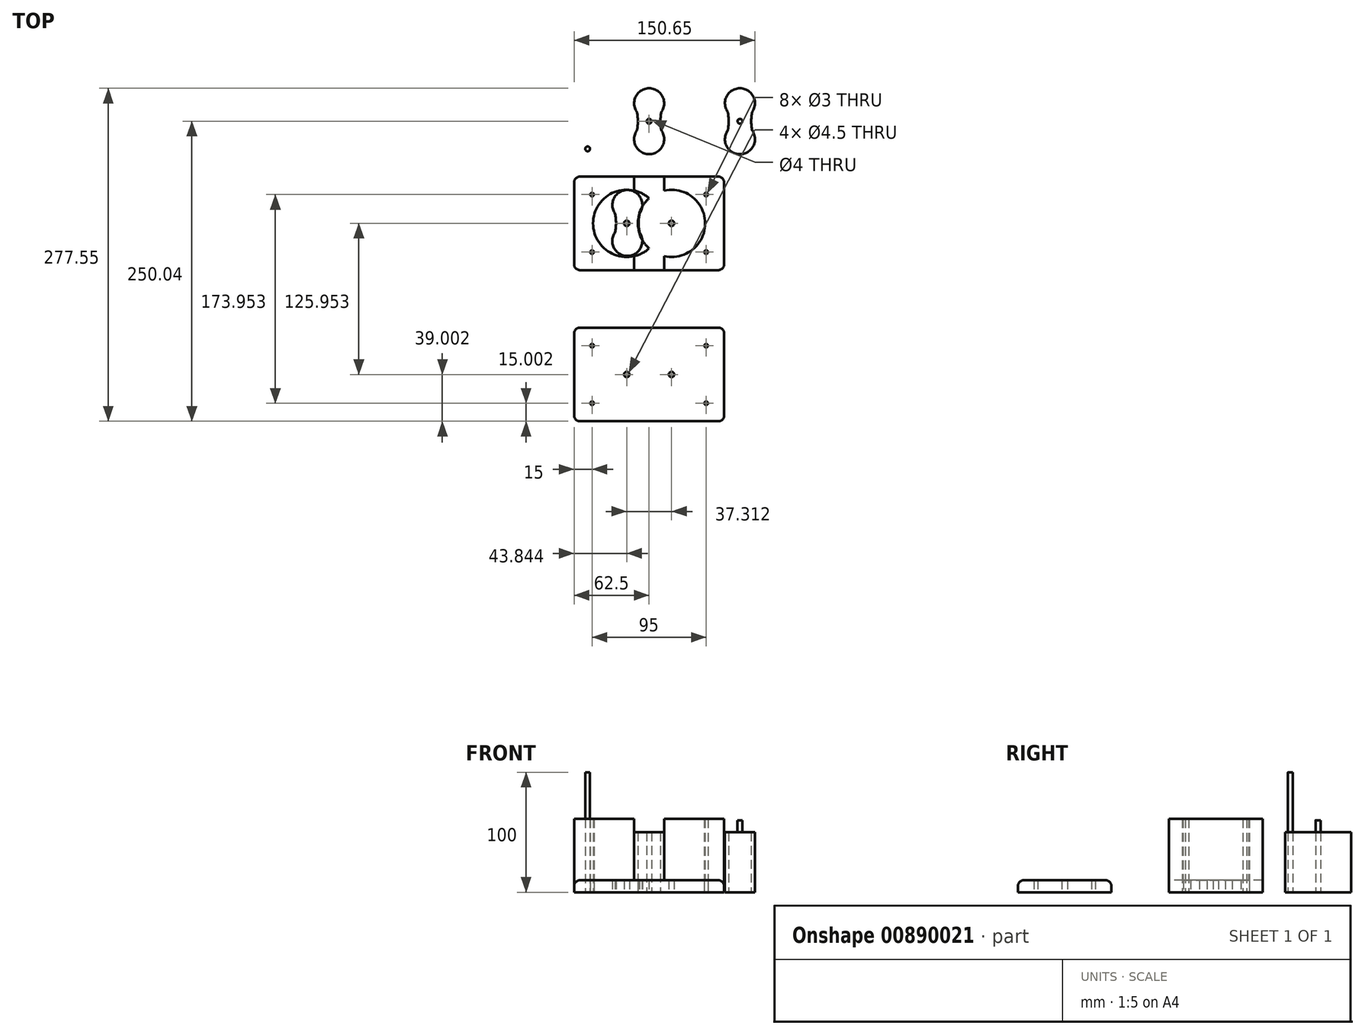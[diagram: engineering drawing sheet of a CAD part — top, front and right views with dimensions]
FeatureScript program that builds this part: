
annotation { "Feature Type Name" : "Feature", "Feature Type Description" : "" }
export const myFeature = defineFeature(function(context is Context, id is Id, definition is map)
    precondition{}
    {
        {
            var Q0;
            Q0=qCreatedBy(makeId("Top.planeOp"),FACE);
            var sketch = newSketch(context, id + "F0", { "sketchPlane" : qUnion([Q0])});
            skArc(sketch, "E0", {"start": v(-10.1, -7.63) * mm, "mid": v(0, -27.5) * mm, "end": v(10.1, -7.63) * mm});
            skArc(sketch, "E1", {"start": v(10.1, 7.63) * mm, "mid": v(0, 27.5) * mm, "end": v(-10.1, 7.64) * mm});
            skLineSegment(sketch, "E2", {"start": v(0, 107.1) * mm, "end": v(0, -296.82) * mm, "construction": true});
            skArc(sketch, "E3", {"start": v(10.1, 7.63) * mm, "mid": v(9.42, 0) * mm, "end": v(10.1, -7.63) * mm});
            skArc(sketch, "E4.trimOffspring", {"start": v(-10.1, -7.63) * mm, "mid": v(-9.43, 0) * mm, "end": v(-10.1, 7.64) * mm});
            skPoint(sketch, "E5.center.orphan", {"position": v(-53, 0) * mm});
            skCircle(sketch, "E6", {"center": v(18.66, -85.09) * mm, "radius": 28 * mm});
            skCircle(sketch, "E7", {"center": v(-18.66, -85.09) * mm, "radius": 28 * mm});
            skLineSegment(sketch, "E8.bottom", {"start": v(62.5, -46.09) * mm, "end": v(-62.5, -46.09) * mm});
            skLineSegment(sketch, "E8.top", {"start": v(62.5, -124.09) * mm, "end": v(-62.5, -124.09) * mm});
            skLineSegment(sketch, "E8.left", {"start": v(62.5, -46.09) * mm, "end": v(62.5, -124.09) * mm});
            skLineSegment(sketch, "E8.right", {"start": v(-62.5, -46.09) * mm, "end": v(-62.5, -124.09) * mm});
            skLineSegment(sketch, "E9", {"start": v(46.66, -85.09) * mm, "end": v(62.5, -85.09) * mm, "construction": true});
            skLineSegment(sketch, "E10", {"start": v(-46.66, -85.09) * mm, "end": v(-62.5, -85.09) * mm, "construction": true});
            skLineSegment(sketch, "E11", {"start": v(-12.5, -57.77) * mm, "end": v(-12.5, -46.09) * mm});
            skLineSegment(sketch, "E12", {"start": v(12.5, -46.09) * mm, "end": v(12.5, -57.77) * mm});
            skLineSegment(sketch, "E13", {"start": v(12.5, -112.4) * mm, "end": v(12.5, -124.09) * mm});
            skLineSegment(sketch, "E14", {"start": v(-12.5, -112.4) * mm, "end": v(-12.5, -124.09) * mm});
            skCircle(sketch, "E15", {"center": v(-18.66, -85.09) * mm, "radius": 2.25 * mm});
            skCircle(sketch, "E16", {"center": v(18.66, -85.09) * mm, "radius": 2.25 * mm});
            skCircle(sketch, "E17", {"center": v(0, 0) * mm, "radius": 2 * mm});
            skCircle(sketch, "E18", {"center": v(-51.22, -23.03) * mm, "radius": 2 * mm});
            skLineSegment(sketch, "E19.bottom", {"start": v(62.5, -172.04) * mm, "end": v(-62.5, -172.04) * mm});
            skLineSegment(sketch, "E19.top", {"start": v(62.5, -250.04) * mm, "end": v(-62.5, -250.04) * mm});
            skLineSegment(sketch, "E19.left", {"start": v(62.5, -172.04) * mm, "end": v(62.5, -250.04) * mm});
            skLineSegment(sketch, "E19.right", {"start": v(-62.5, -172.04) * mm, "end": v(-62.5, -250.04) * mm});
            skPoint(sketch, "E20", {"position": v(-47.5, -187.04) * mm});
            skPoint(sketch, "E21", {"position": v(-47.5, -235.04) * mm});
            skPoint(sketch, "E22", {"position": v(47.5, -187.04) * mm});
            skPoint(sketch, "E23", {"position": v(47.5, -235.04) * mm});
            skCircle(sketch, "E24", {"center": v(-47.5, -187.04) * mm, "radius": 1.5 * mm});
            skCircle(sketch, "E25", {"center": v(-47.5, -235.04) * mm, "radius": 1.5 * mm});
            skCircle(sketch, "E26", {"center": v(47.5, -187.04) * mm, "radius": 1.5 * mm});
            skCircle(sketch, "E27", {"center": v(47.5, -235.04) * mm, "radius": 1.5 * mm});
            skCircle(sketch, "E28", {"center": v(-47.5, -109.09) * mm, "radius": 1.5 * mm});
            skCircle(sketch, "E29", {"center": v(-47.5, -61.09) * mm, "radius": 1.5 * mm});
            skCircle(sketch, "E30", {"center": v(47.5, -109.09) * mm, "radius": 1.5 * mm});
            skCircle(sketch, "E31", {"center": v(47.5, -61.09) * mm, "radius": 1.5 * mm});
            skCircle(sketch, "E32", {"center": v(-18.66, -211.04) * mm, "radius": 2.25 * mm});
            skPoint(sketch, "E32.centerSnap0", {"position": v(-62.5, -211.04) * mm});
            skCircle(sketch, "E33", {"center": v(18.66, -211.04) * mm, "radius": 2.25 * mm});
            skPoint(sketch, "E33.centerSnap0", {"position": v(62.5, -211.04) * mm});
            skArc(sketch, "E34", {"start": v(65.55, -7.62) * mm, "mid": v(75.65, -27.49) * mm, "end": v(85.75, -7.62) * mm});
            skArc(sketch, "E35", {"start": v(85.75, 7.64) * mm, "mid": v(75.66, 27.51) * mm, "end": v(65.55, 7.65) * mm});
            skArc(sketch, "E36", {"start": v(85.75, 7.64) * mm, "mid": v(85.08, 0.01) * mm, "end": v(85.75, -7.62) * mm});
            skArc(sketch, "E37.trimOffspring", {"start": v(65.55, -7.62) * mm, "mid": v(66.23, 0.02) * mm, "end": v(65.55, 7.65) * mm});
            skCircle(sketch, "E38", {"center": v(75.65, 0) * mm, "radius": 2 * mm});
            skPoint(sketch, "E39", {"position": v(12.5, -85.09) * mm});
            skArc(sketch, "E40", {"start": v(-28.25, -92.43) * mm, "mid": v(-18.16, -112.3) * mm, "end": v(-8.06, -92.43) * mm});
            skArc(sketch, "E41", {"start": v(-8.05, -77.16) * mm, "mid": v(-18.16, -57.3) * mm, "end": v(-28.26, -77.16) * mm});
            skArc(sketch, "E42", {"start": v(-8.05, -77.16) * mm, "mid": v(-8.73, -84.8) * mm, "end": v(-8.06, -92.43) * mm});
            skArc(sketch, "E43.trimOffspring", {"start": v(-28.25, -92.43) * mm, "mid": v(-27.58, -84.8) * mm, "end": v(-28.26, -77.16) * mm});
            skLineSegment(sketch, "E44", {"start": v(-18.16, -57.3) * mm, "end": v(-18.16, -55.1) * mm});
            skPoint(sketch, "E44.startSnap0", {"position": v(-18.16, -57.3) * mm});
            skLineSegment(sketch, "E45", {"start": v(-18.16, -112.3) * mm, "end": v(-18.16, -113.54) * mm});
            skSolve(sketch);
        }
        {
            var Q0;
            Q0=makeQuery(id+"F0.imprint","IMPRINT",FACE,{"disambiguationData":[TD([[makeQuery(id+"F0.imprint","IMPRINT",EDGE,{"derivedFrom":sQuery(id+"F0.wireOp",EDGE,"E0")}),1.0]])]});
            var Q1;
            Q1=makeQuery(id+"F0.imprint","IMPRINT",FACE,{"disambiguationData":[TD([[makeQuery(id+"F0.imprint","IMPRINT",EDGE,{"derivedFrom":sQuery(id+"F0.wireOp",EDGE,"E34")}),1.0]])]});
            extrude(context, id + "F1", {"entities" : qUnion([Q0, Q1]), "depth" : 50 * mm, "offsetDistance" : 25 * mm});
        }
        {
            var Q0;
            Q0=makeQuery(id+"F0.imprint","IMPRINT",FACE,{"disambiguationData":[TD([[makeQuery(id+"F0.imprint","IMPRINT",EDGE,{"derivedFrom":sQuery(id+"F0.wireOp",EDGE,"E38")}),1.0]])]});
            extrude(context, id + "F2", {"entities" : qUnion([Q0]), "operationType" : NewBodyOperationType.ADD, "depth" : 60 * mm, "offsetDistance" : 25 * mm});
        }
        {
            var Q0;
            Q0=makeQuery(id+"F1.opExtrude","SWEPT_EDGE",EDGE,{"disambiguationData":[OSD([sQuery(id+"F0.wireOp",EDGE,"E1"),sQuery(id+"F0.wireOp",EDGE,"E3")])]});
            var Q1;
            Q1=makeQuery(id+"F1.opExtrude","SWEPT_EDGE",EDGE,{"disambiguationData":[OSD([sQuery(id+"F0.wireOp",EDGE,"E0"),sQuery(id+"F0.wireOp",EDGE,"E3")])]});
            var Q2;
            Q2=makeQuery(id+"F1.opExtrude","SWEPT_EDGE",EDGE,{"disambiguationData":[OSD([sQuery(id+"F0.wireOp",EDGE,"E0"),sQuery(id+"F0.wireOp",EDGE,"E4.trimOffspring")])]});
            var Q3;
            Q3=makeQuery(id+"F1.opExtrude","SWEPT_EDGE",EDGE,{"disambiguationData":[OSD([sQuery(id+"F0.wireOp",EDGE,"E1"),sQuery(id+"F0.wireOp",EDGE,"E4.trimOffspring")])]});
            var Q4;
            Q4=makeQuery(id+"F1.opExtrude","SWEPT_EDGE",EDGE,{"disambiguationData":[OSD([sQuery(id+"F0.wireOp",EDGE,"E34"),sQuery(id+"F0.wireOp",EDGE,"E36")])]});
            var Q5;
            Q5=makeQuery(id+"F1.opExtrude","SWEPT_EDGE",EDGE,{"disambiguationData":[OSD([sQuery(id+"F0.wireOp",EDGE,"E35"),sQuery(id+"F0.wireOp",EDGE,"E36")])]});
            var Q6;
            Q6=makeQuery(id+"F1.opExtrude","SWEPT_EDGE",EDGE,{"disambiguationData":[OSD([sQuery(id+"F0.wireOp",EDGE,"E34"),sQuery(id+"F0.wireOp",EDGE,"E37.trimOffspring")])]});
            var Q7;
            Q7=makeQuery(id+"F1.opExtrude","SWEPT_EDGE",EDGE,{"disambiguationData":[OSD([sQuery(id+"F0.wireOp",EDGE,"E35"),sQuery(id+"F0.wireOp",EDGE,"E37.trimOffspring")])]});
            fillet(context, id + "F3", {"entities" : qUnion([Q0, Q1, Q2, Q3, Q4, Q5, Q6, Q7]), "radius" : 5 * mm, "tangentPropagation" : true, "allowEdgeOverflow" : false});
        }
        {
            var Q0;
            Q0=makeQuery(id+"F0.imprint","IMPRINT",FACE,{"disambiguationData":[TD([[makeQuery(id+"F0.imprint","IMPRINT",EDGE,{"derivedFrom":sQuery(id+"F0.wireOp",EDGE,"E15")}),-1.0]])]});
            var Q1;
            {var subQ0=sQuery(id+"F0.wireOp",EDGE,"E7");var subQ1=sQuery(id+"F0.wireOp",EDGE,"E6");var subQ2=makeQuery(id+"F0.imprint","INTERSECT",VERTEX,{"disambiguationData":[OD(0.0)],"derivedFrom":[subQ1,subQ0]});Q1=makeQuery(id+"F0.imprint","IMPRINT",FACE,{"disambiguationData":[TD([[makeQuery(id+"F0.imprint","IMPRINT",EDGE,{"disambiguationData":[TD([[subQ2,-1.0]])],"derivedFrom":subQ1}),1.0]])]});}
            var Q2;
            Q2=makeQuery(id+"F0.imprint","IMPRINT",FACE,{"disambiguationData":[TD([[makeQuery(id+"F0.imprint","IMPRINT",EDGE,{"derivedFrom":sQuery(id+"F0.wireOp",EDGE,"E16")}),-1.0]])]});
            var Q3;
            {var subQ0=sQuery(id+"F0.wireOp",EDGE,"E13");Q3=makeQuery(id+"F0.imprint","IMPRINT",FACE,{"disambiguationData":[TD([[makeQuery(id+"F0.imprint","IMPRINT",EDGE,{"derivedFrom":subQ0}),-1.0]])]});}
            var Q4;
            {var subQ0=sQuery(id+"F0.wireOp",EDGE,"E11");Q4=makeQuery(id+"F0.imprint","IMPRINT",FACE,{"disambiguationData":[TD([[makeQuery(id+"F0.imprint","IMPRINT",EDGE,{"derivedFrom":subQ0}),-1.0]])]});}
            var Q5;
            Q5=makeQuery(id+"F0.imprint","IMPRINT",FACE,{"disambiguationData":[TD([[makeQuery(id+"F0.imprint","IMPRINT",EDGE,{"derivedFrom":sQuery(id+"F0.wireOp",EDGE,"E19.bottom")}),1.0]])]});
            extrude(context, id + "F4", {"entities" : qUnion([Q0, Q1, Q2, Q3, Q4, Q5]), "depth" : 10 * mm, "offsetDistance" : 25 * mm});
        }
        {
            var Q0;
            {var subQ0=sQuery(id+"F0.wireOp",EDGE,"E8.right");Q0=makeQuery(id+"F0.imprint","IMPRINT",FACE,{"disambiguationData":[TD([[makeQuery(id+"F0.imprint","IMPRINT",EDGE,{"derivedFrom":subQ0}),1.0]])]});}
            var Q1;
            {var subQ0=sQuery(id+"F0.wireOp",EDGE,"E8.left");Q1=makeQuery(id+"F0.imprint","IMPRINT",FACE,{"disambiguationData":[TD([[makeQuery(id+"F0.imprint","IMPRINT",EDGE,{"derivedFrom":subQ0}),-1.0]])]});}
            extrude(context, id + "F5", {"entities" : qUnion([Q0, Q1]), "operationType" : NewBodyOperationType.ADD, "depth" : 61 * mm, "offsetDistance" : 25 * mm});
        }
        {
            var Q0;
            Q0=makeQuery(id+"F0.imprint","IMPRINT",FACE,{"disambiguationData":[TD([[makeQuery(id+"F0.imprint","IMPRINT",EDGE,{"derivedFrom":sQuery(id+"F0.wireOp",EDGE,"E18")}),1.0]])]});
            extrude(context, id + "F6", {"entities" : qUnion([Q0]), "depth" : 100 * mm, "offsetDistance" : 25 * mm});
        }
        {
            var Q0;
            Q0=makeQuery(id+"F4.opExtrude","CAP_EDGE",EDGE,{"disambiguationData":[OSD([sQuery(id+"F0.wireOp",EDGE,"E19.right")])],"isStart":false});
            var Q1;
            Q1=makeQuery(id+"F4.opExtrude","CAP_EDGE",EDGE,{"disambiguationData":[OSD([sQuery(id+"F0.wireOp",EDGE,"E19.bottom")])],"isStart":false});
            var Q2;
            Q2=makeQuery(id+"F4.opExtrude","CAP_EDGE",EDGE,{"disambiguationData":[OSD([sQuery(id+"F0.wireOp",EDGE,"E19.top")])],"isStart":false});
            var Q3;
            Q3=makeQuery(id+"F4.opExtrude","CAP_EDGE",EDGE,{"disambiguationData":[OSD([sQuery(id+"F0.wireOp",EDGE,"E19.left")])],"isStart":false});
            fillet(context, id + "F7", {"entities" : qUnion([Q0, Q1, Q2, Q3]), "radius" : 5 * mm, "tangentPropagation" : true, "allowEdgeOverflow" : false});
        }
        {
            var Q0;
            Q0=makeQuery(id+"F7.opFillet","BLEND_EDGE",EDGE,{"blendedFrom":[makeQuery(id+"F4.opExtrude","CAP_EDGE",EDGE,{"disambiguationData":[OSD([sQuery(id+"F0.wireOp",EDGE,"E19.bottom")])],"isStart":false}),makeQuery(id+"F4.opExtrude","CAP_EDGE",EDGE,{"disambiguationData":[OSD([sQuery(id+"F0.wireOp",EDGE,"E19.right")])],"isStart":false})],"blendedInto":[]});
            var Q1;
            Q1=makeQuery(id+"F7.opFillet","BLEND_EDGE",EDGE,{"blendedFrom":[makeQuery(id+"F4.opExtrude","CAP_EDGE",EDGE,{"disambiguationData":[OSD([sQuery(id+"F0.wireOp",EDGE,"E19.top")])],"isStart":false}),makeQuery(id+"F4.opExtrude","CAP_EDGE",EDGE,{"disambiguationData":[OSD([sQuery(id+"F0.wireOp",EDGE,"E19.right")])],"isStart":false})],"blendedInto":[]});
            var Q2;
            Q2=makeQuery(id+"F7.opFillet","BLEND_EDGE",EDGE,{"blendedFrom":[makeQuery(id+"F4.opExtrude","CAP_EDGE",EDGE,{"disambiguationData":[OSD([sQuery(id+"F0.wireOp",EDGE,"E19.top")])],"isStart":false}),makeQuery(id+"F4.opExtrude","CAP_EDGE",EDGE,{"disambiguationData":[OSD([sQuery(id+"F0.wireOp",EDGE,"E19.left")])],"isStart":false})],"blendedInto":[]});
            var Q3;
            Q3=makeQuery(id+"F7.opFillet","BLEND_EDGE",EDGE,{"blendedFrom":[makeQuery(id+"F4.opExtrude","CAP_EDGE",EDGE,{"disambiguationData":[OSD([sQuery(id+"F0.wireOp",EDGE,"E19.bottom")])],"isStart":false}),makeQuery(id+"F4.opExtrude","CAP_EDGE",EDGE,{"disambiguationData":[OSD([sQuery(id+"F0.wireOp",EDGE,"E19.left")])],"isStart":false})],"blendedInto":[]});
            fillet(context, id + "F8", {"entities" : qUnion([Q0, Q1, Q2, Q3]), "radius" : 5 * mm, "tangentPropagation" : true, "allowEdgeOverflow" : false});
        }
        {
            var Q0;
            Q0=makeQuery(id+"F5.opExtrude","SWEPT_EDGE",EDGE,{"disambiguationData":[OSD([sQuery(id+"F0.wireOp",EDGE,"E8.bottom"),sQuery(id+"F0.wireOp",EDGE,"E8.right")])]});
            var Q1;
            Q1=makeQuery(id+"F5.opExtrude","SWEPT_EDGE",EDGE,{"disambiguationData":[OSD([sQuery(id+"F0.wireOp",EDGE,"E8.top"),sQuery(id+"F0.wireOp",EDGE,"E8.right")])]});
            var Q2;
            Q2=makeQuery(id+"F5.opExtrude","SWEPT_EDGE",EDGE,{"disambiguationData":[OSD([sQuery(id+"F0.wireOp",EDGE,"E8.bottom"),sQuery(id+"F0.wireOp",EDGE,"E8.left")])]});
            var Q3;
            Q3=makeQuery(id+"F5.opExtrude","SWEPT_EDGE",EDGE,{"disambiguationData":[OSD([sQuery(id+"F0.wireOp",EDGE,"E8.top"),sQuery(id+"F0.wireOp",EDGE,"E8.left")])]});
            fillet(context, id + "F9", {"entities" : qUnion([Q0, Q1, Q2, Q3]), "radius" : 5 * mm, "tangentPropagation" : true, "allowEdgeOverflow" : false});
        }
    });
